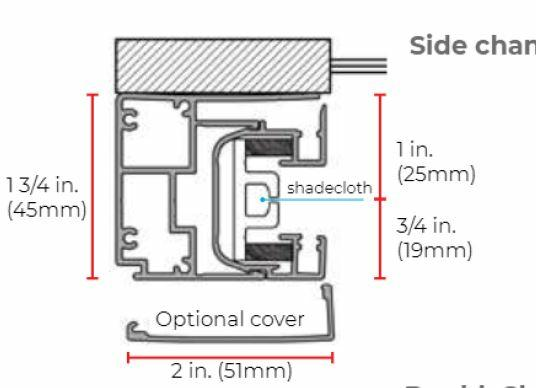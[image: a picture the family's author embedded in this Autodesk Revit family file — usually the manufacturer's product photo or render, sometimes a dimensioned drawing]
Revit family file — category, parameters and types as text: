
# Revit family: ShadeLoc-Wall_Mount
name_source: partatom
category: Specialty Equipment
units: mm (PartAtom-declared; Revit-internal decimal feet)

## family parameters
Always vertical = Yes
Cut with Voids When Loaded = No
Enable Cutting in Views = No
Host = Wall
Maintain Annotation Orientation = No
Part Type = Normal
Room Calculation Point = No
Round Connector Dimension = Use Diameter
Shared = No

## types (1)
- ShadeLoc-Wall_Mount
    Default Elevation = 0' - 0"
    Description = Wall Mount
    End Caps = Yes
    Exposed Hembar = Yes
    Exposed Hembar Material = Metal - Mecho - Aluminum - White
    Fascia Material = Metal - Mecho - Aluminum - White
    Manufacturer = Mecho
    Model = Shadeloc
    Product Documentation URL = https://www.mechoshade.com
    Shade Cloth = 0' - 10 1/8"
    Shadecloth Material = Fabric - Mecho - 0701 White
    Side Channel = Yes
    Track Material = Metal - Mecho - Aluminum - White
    URL = https://www.mechoshade.com
    Visible Fabric Height = 0' - 0"

## geometry (parser evidence)
native form markers: Sweep x19
no freeform markers — native parametric forms only
